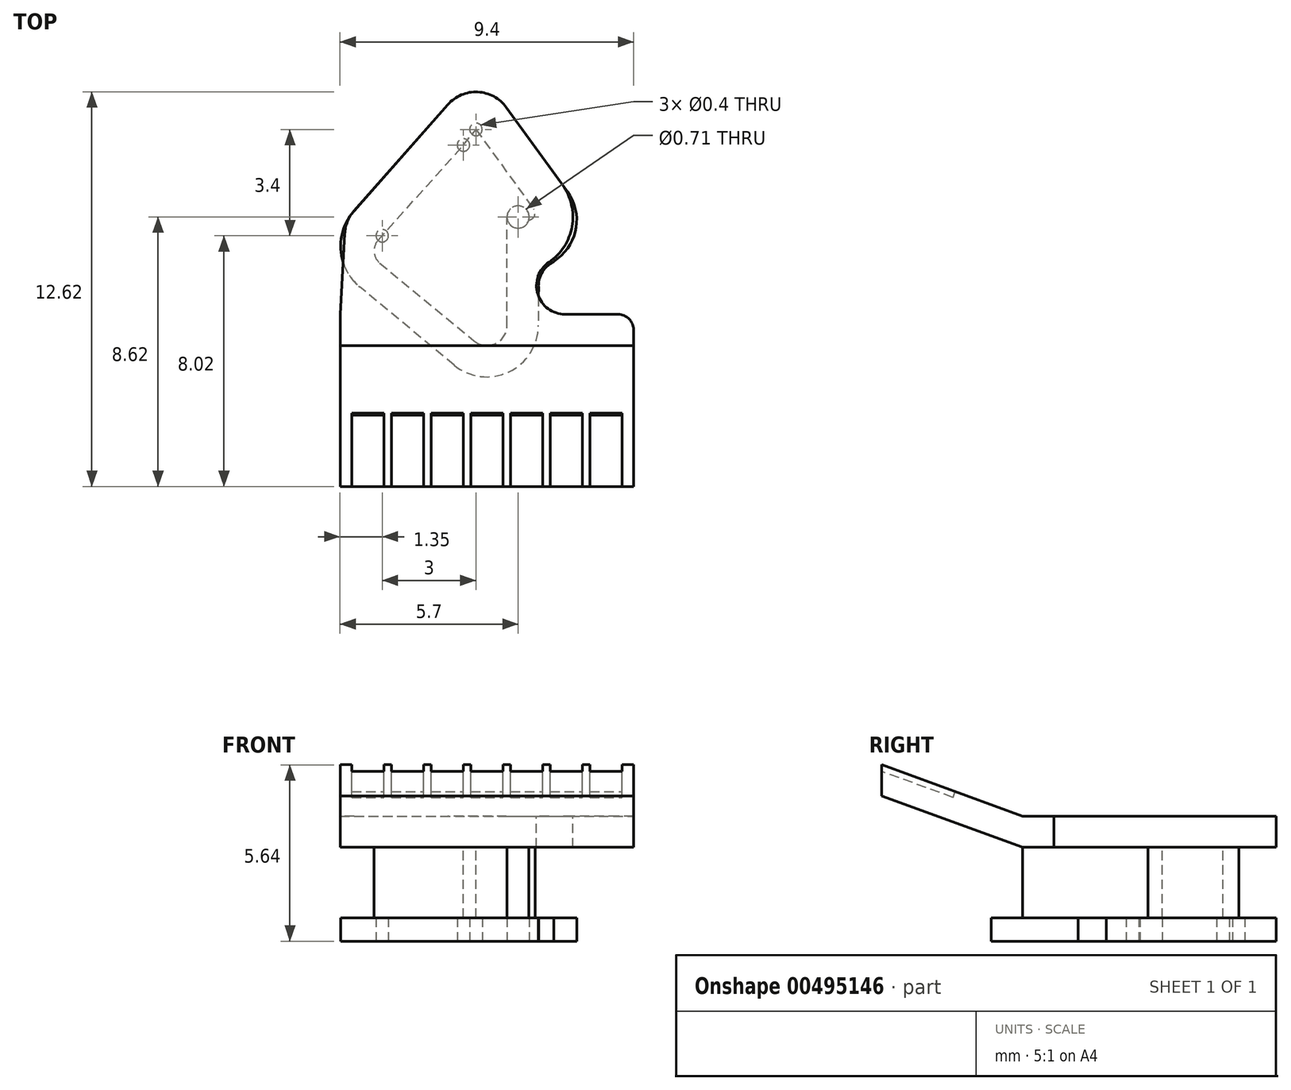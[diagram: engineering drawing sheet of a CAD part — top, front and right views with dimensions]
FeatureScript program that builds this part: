
annotation { "Feature Type Name" : "Feature", "Feature Type Description" : "" }
export const myFeature = defineFeature(function(context is Context, id is Id, definition is map)
    precondition{}
    {
        {
            assignVariable(context, id + "F0", {"name" : "top_height", "anyValue" : 1 * mm});
        }
        {
            assignVariable(context, id + "F1", {"name" : "foot_height", "anyValue" : 0.75 * mm});
        }
        {
            assignVariable(context, id + "F2", {"name" : "total_height", "anyValue" : 4 * mm});
        }
        {
            var Q0;
            Q0=qCreatedBy(makeId("Top.planeOp"),FACE);
            var sketch = newSketch(context, id + "F3", { "sketchPlane" : qUnion([Q0])});
            skCircle(sketch, "E0", {"center": v(-3.35, -1) * mm, "radius": 0.2 * mm});
            skCircle(sketch, "E1", {"center": v(-0.75, 1.9) * mm, "radius": 0.2 * mm});
            skCircle(sketch, "E2", {"center": v(-0.35, 2.4) * mm, "radius": 0.2 * mm});
            skCircle(sketch, "E3", {"center": v(1, -0.4) * mm, "radius": 0.35 * mm});
            skCircle(sketch, "E4", {"center": v(2.5, -2.6) * mm, "radius": 0.85 * mm});
            skSolve(sketch);
        }
        {
            var Q0;
            Q0=qSketchRegion(id+"F3",true);
            extrude(context, id + "F4", {"entities" : qUnion([Q0]), "depth" : getVariable(context, 'total_height')});
        }
        {
            var Q0;
            Q0=makeQuery(id+"F4.opExtrude","CAP_FACE",FACE,{"disambiguationData":[OSD([sQuery(id+"F3.wireOp",EDGE,"E4")])],"isStart":false});
            var sketch = newSketch(context, id + "F5", { "sketchPlane" : qUnion([Q0])});
            skArc(sketch, "E5", {"start": v(2.42, 0.63) * mm, "mid": v(2.72, -0.7) * mm, "end": v(1.99, -1.85) * mm});
            skArc(sketch, "E6", {"start": v(1.99, -1.85) * mm, "mid": v(1.63, -2.87) * mm, "end": v(2.5, -3.51) * mm});
            skArc(sketch, "E7", {"start": v(0.62, 3.1) * mm, "mid": v(-0.3, 3.6) * mm, "end": v(-1.25, 3.2) * mm});
            skArc(sketch, "E8", {"start": v(-4.55, -0.93) * mm, "mid": v(-4.46, -0.54) * mm, "end": v(-4.25, -0.2) * mm});
            skLineSegment(sketch, "E9", {"start": v(-4.25, -0.2) * mm, "end": v(-1.25, 3.2) * mm});
            skLineSegment(sketch, "E10", {"start": v(0.62, 3.1) * mm, "end": v(2.42, 0.63) * mm});
            skLineSegment(sketch, "E11", {"start": v(-4.7, -4.51) * mm, "end": v(4.7, -4.51) * mm});
            skLineSegment(sketch, "E12", {"start": v(-4.7, -4.51) * mm, "end": v(-4.7, -3.51) * mm});
            skLineSegment(sketch, "E13", {"start": v(-4.7, -3.51) * mm, "end": v(-4.55, -0.93) * mm});
            skLineSegment(sketch, "E14", {"start": v(4.7, -4.51) * mm, "end": v(4.7, -4.01) * mm});
            skLineSegment(sketch, "E15", {"start": v(4.2, -3.51) * mm, "end": v(2.5, -3.51) * mm});
            skPoint(sketch, "E16.visualSharp", {"position": v(4.7, -3.51) * mm});
            skArc(sketch, "E16.filletArc", {"start": v(4.7, -4.01) * mm, "mid": v(4.55, -3.66) * mm, "end": v(4.2, -3.51) * mm});
            skLineSegment(sketch, "E17", {"start": v(4.7, -3.51) * mm, "end": v(4.7, -4.51) * mm, "construction": true});
            skSolve(sketch);
        }
        {
            var Q0;
            Q0=qSketchRegion(id+"F5",true);
            extrude(context, id + "F6", {"entities" : qUnion([Q0]), "oppositeDirection" : true, "depth" : getVariable(context, 'top_height')});
        }
        {
            var Q0;
            Q0=makeQuery(id+"F6.opExtrude","CAP_FACE",FACE,{"disambiguationData":[OSD([sQuery(id+"F5.wireOp",EDGE,"E5"),sQuery(id+"F5.wireOp",EDGE,"E6"),sQuery(id+"F5.wireOp",EDGE,"E7"),sQuery(id+"F5.wireOp",EDGE,"E8"),sQuery(id+"F5.wireOp",EDGE,"E9"),sQuery(id+"F5.wireOp",EDGE,"E10"),sQuery(id+"F5.wireOp",EDGE,"E11"),sQuery(id+"F5.wireOp",EDGE,"E12"),sQuery(id+"F5.wireOp",EDGE,"E13"),sQuery(id+"F5.wireOp",EDGE,"E14"),sQuery(id+"F5.wireOp",EDGE,"E15"),sQuery(id+"F5.wireOp",EDGE,"E16.filletArc")])],"isStart":false});
            var sketch = newSketch(context, id + "F7", { "sketchPlane" : qUnion([Q0])});
            skArc(sketch, "E18", {"start": v(-0.41, 4.36) * mm, "mid": v(0.27, 4.45) * mm, "end": v(0.64, 3.87) * mm});
            skLineSegment(sketch, "E19", {"start": v(0.64, 3.87) * mm, "end": v(0.64, 0.4) * mm});
            skArc(sketch, "E20", {"start": v(0.64, 0.4) * mm, "mid": v(1.05, 0.05) * mm, "end": v(1.34, 0.5) * mm});
            skLineSegment(sketch, "E21", {"start": v(-3.48, 1.15) * mm, "end": v(-0.75, -1.9) * mm});
            skPoint(sketch, "E22", {"position": v(-3.35, 1) * mm});
            skPoint(sketch, "E23", {"position": v(-0.75, -1.9) * mm});
            skPoint(sketch, "E24", {"position": v(-0.35, -2.4) * mm});
            skLineSegment(sketch, "E25", {"start": v(-0.75, -1.9) * mm, "end": v(-0.35, -2.4) * mm});
            skArc(sketch, "E26", {"start": v(-3.48, 1.15) * mm, "mid": v(-3.6, 1.52) * mm, "end": v(-3.43, 1.87) * mm});
            skLineSegment(sketch, "E27", {"start": v(-3.43, 1.87) * mm, "end": v(-0.41, 4.36) * mm});
            skLineSegment(sketch, "E28", {"start": v(-0.35, -2.4) * mm, "end": v(1.5, 0.15) * mm});
            skArc(sketch, "E29", {"start": v(1.5, 0.15) * mm, "mid": v(1.52, 0.37) * mm, "end": v(1.34, 0.5) * mm});
            skSolve(sketch);
        }
        {
            var Q0;
            Q0=qSketchRegion(id+"F7",true);
            extrude(context, id + "F8", {"entities" : qUnion([Q0]), "depth" : getVariable(context, 'total_height') - getVariable(context, 'top_height') - getVariable(context, 'foot_height')});
        }
        {
            var Q0;
            Q0=makeQuery(id+"F8.opExtrude","CAP_FACE",FACE,{"disambiguationData":[OSD([sQuery(id+"F7.wireOp",EDGE,"E18"),sQuery(id+"F7.wireOp",EDGE,"E19"),sQuery(id+"F7.wireOp",EDGE,"E20"),sQuery(id+"F7.wireOp",EDGE,"E21"),sQuery(id+"F7.wireOp",EDGE,"E25"),sQuery(id+"F7.wireOp",EDGE,"E26"),sQuery(id+"F7.wireOp",EDGE,"E27"),sQuery(id+"F7.wireOp",EDGE,"N2l6SWo4-kHqm-KqNM-dVRS-lvh92gExjqxJ"),sQuery(id+"F7.wireOp",EDGE,"E28"),sQuery(id+"F7.wireOp",EDGE,"JDNASti5-YGJY-wVQ3-qJS6-gXQv6eLAw1aX")])],"isStart":false});
            var sketch = newSketch(context, id + "F9", { "sketchPlane" : qUnion([Q0])});
            skLineSegment(sketch, "E30", {"start": v(-4.26, 0.21) * mm, "end": v(-1.25, -3.2) * mm});
            skLineSegment(sketch, "E31", {"start": v(0.62, -3.1) * mm, "end": v(2.58, -0.4) * mm});
            skLineSegment(sketch, "E32", {"start": v(1.65, 2.96) * mm, "end": v(1.65, 3.87) * mm});
            skLineSegment(sketch, "E33", {"start": v(-1.05, 5.14) * mm, "end": v(-4.07, 2.64) * mm});
            skArc(sketch, "E34.filletArc", {"start": v(-4.07, 2.64) * mm, "mid": v(-4.68, 1.47) * mm, "end": v(-4.26, 0.21) * mm});
            skPoint(sketch, "E35.visualSharp", {"position": v(1.65, 7.36) * mm});
            skArc(sketch, "E35.filletArc", {"start": v(1.65, 3.87) * mm, "mid": v(0.7, 5.36) * mm, "end": v(-1.05, 5.14) * mm});
            skArc(sketch, "E36.filletArc", {"start": v(2.58, -0.4) * mm, "mid": v(2.86, 0.73) * mm, "end": v(2.26, 1.73) * mm});
            skArc(sketch, "E37.filletArc", {"start": v(1.65, 2.96) * mm, "mid": v(1.8, 2.27) * mm, "end": v(2.26, 1.73) * mm});
            skPoint(sketch, "E38.visualSharp", {"position": v(-0.26, -4.32) * mm});
            skArc(sketch, "E38.filletArc", {"start": v(-1.25, -3.2) * mm, "mid": v(-0.3, -3.6) * mm, "end": v(0.62, -3.1) * mm});
            skSolve(sketch);
        }
        {
            var Q0;
            Q0=qSketchRegion(id+"F9",true);
            extrude(context, id + "F10", {"entities" : qUnion([Q0]), "depth" : getVariable(context, 'foot_height')});
        }
        {
            var Q0;
            Q0=makeQuery(id+"F4.opExtrude","SWEPT_BODY",BODY,{"disambiguationData":[OSD([sQuery(id+"F3.wireOp",EDGE,"E0")])]});
            var Q1;
            Q1=makeQuery(id+"F4.opExtrude","SWEPT_BODY",BODY,{"disambiguationData":[OSD([sQuery(id+"F3.wireOp",EDGE,"E1")])]});
            var Q2;
            Q2=makeQuery(id+"F4.opExtrude","SWEPT_BODY",BODY,{"disambiguationData":[OSD([sQuery(id+"F3.wireOp",EDGE,"E2")])]});
            var Q3;
            Q3=makeQuery(id+"F4.opExtrude","SWEPT_BODY",BODY,{"disambiguationData":[OSD([sQuery(id+"F3.wireOp",EDGE,"E3")])]});
            var Q4;
            Q4=makeQuery(id+"F4.opExtrude","SWEPT_BODY",BODY,{"disambiguationData":[OSD([sQuery(id+"F3.wireOp",EDGE,"E4")])]});
            var Q5;
            Q5=makeQuery(id+"F10.opExtrude","SWEPT_BODY",BODY,{"disambiguationData":[OSD([sQuery(id+"F9.wireOp",EDGE,"E30"),sQuery(id+"F9.wireOp",EDGE,"E31"),sQuery(id+"F9.wireOp",EDGE,"E32"),sQuery(id+"F9.wireOp",EDGE,"E33"),sQuery(id+"F9.wireOp",EDGE,"E34.filletArc"),sQuery(id+"F9.wireOp",EDGE,"E35.filletArc"),sQuery(id+"F9.wireOp",EDGE,"E36.filletArc"),sQuery(id+"F9.wireOp",EDGE,"E37.filletArc"),sQuery(id+"F9.wireOp",EDGE,"E38.filletArc")])]});
            booleanBodies(context, id + "F11", {"operationType" : BooleanOperationType.SUBTRACTION, "tools" : qUnion([Q0, Q1, Q2, Q3, Q4]), "targets" : qUnion([Q5])});
        }
        {
            var Q0;
            Q0=qCreatedBy(makeId("Right.planeOp"),FACE);
            var sketch = newSketch(context, id + "F12", { "sketchPlane" : qUnion([Q0])});
            skLineSegment(sketch, "E39", {"start": v(-9.02, 5.64) * mm, "end": v(-4.51, 4) * mm});
            skSolve(sketch);
        }
        {
            var Q0;
            Q0=makeQuery(id+"F6.opExtrude","SWEPT_FACE",FACE,{"disambiguationData":[OSD([sQuery(id+"F5.wireOp",EDGE,"E11")])]});
            var Q1;
            Q1=sQuery(id+"F12.wireOp",EDGE,"E39");
            sweep(context, id + "F13", {"operationType" : NewBodyOperationType.ADD, "profiles" : qUnion([Q0]), "path" : qUnion([Q1]), "keepProfileOrientation" : true});
        }
        {
            var Q0;
            {var subQ0=sQuery(id+"F12.wireOp",EDGE,"E39");var subQ1=sQuery(id+"F5.wireOp",EDGE,"E11");Q0=makeQuery(id+"F13.opSweep","SWEPT_FACE",FACE,{"disambiguationData":[OSD([subQ1,subQ0]),TDD([makeQuery(id+"F6.opExtrude","CAP_EDGE",EDGE,{"disambiguationData":[OSD([subQ1])],"isStart":true}),subQ0])]});}
            var sketch = newSketch(context, id + "F14", { "sketchPlane" : qUnion([Q0])});
            skLineSegment(sketch, "E40.bottom", {"start": v(-4.32, -7.9) * mm, "end": v(-3.3, -7.9) * mm});
            skLineSegment(sketch, "E40.top", {"start": v(-4.32, -10.4) * mm, "end": v(-3.3, -10.4) * mm});
            skLineSegment(sketch, "E40.left", {"start": v(-4.32, -7.9) * mm, "end": v(-4.32, -10.4) * mm});
            skLineSegment(sketch, "E40.right", {"start": v(-3.3, -7.9) * mm, "end": v(-3.3, -10.4) * mm});
            skLineSegment(sketch, "E41.1.0.0", {"start": v(-3.05, -7.9) * mm, "end": v(-3.05, -10.4) * mm});
            skLineSegment(sketch, "E41.1.0.1", {"start": v(-3.05, -7.9) * mm, "end": v(-2.03, -7.9) * mm});
            skLineSegment(sketch, "E41.1.0.2", {"start": v(-2.03, -7.9) * mm, "end": v(-2.03, -10.4) * mm});
            skLineSegment(sketch, "E41.1.0.3", {"start": v(-3.05, -10.4) * mm, "end": v(-2.03, -10.4) * mm});
            skLineSegment(sketch, "E41.2.0.0", {"start": v(-1.78, -7.9) * mm, "end": v(-1.78, -10.4) * mm});
            skLineSegment(sketch, "E41.2.0.1", {"start": v(-1.78, -7.9) * mm, "end": v(-0.76, -7.9) * mm});
            skLineSegment(sketch, "E41.2.0.2", {"start": v(-0.76, -7.9) * mm, "end": v(-0.76, -10.4) * mm});
            skLineSegment(sketch, "E41.2.0.3", {"start": v(-1.78, -10.4) * mm, "end": v(-0.76, -10.4) * mm});
            skLineSegment(sketch, "E41.3.0.0", {"start": v(-0.51, -7.9) * mm, "end": v(-0.51, -10.4) * mm});
            skLineSegment(sketch, "E41.3.0.1", {"start": v(-0.5, -7.9) * mm, "end": v(0.51, -7.9) * mm});
            skLineSegment(sketch, "E41.3.0.2", {"start": v(0.51, -7.9) * mm, "end": v(0.51, -10.4) * mm});
            skLineSegment(sketch, "E41.3.0.3", {"start": v(-0.5, -10.4) * mm, "end": v(0.51, -10.4) * mm});
            skLineSegment(sketch, "E41.4.0.0", {"start": v(0.76, -7.9) * mm, "end": v(0.76, -10.4) * mm});
            skLineSegment(sketch, "E41.4.0.1", {"start": v(0.76, -7.9) * mm, "end": v(1.78, -7.9) * mm});
            skLineSegment(sketch, "E41.4.0.2", {"start": v(1.78, -7.9) * mm, "end": v(1.78, -10.4) * mm});
            skLineSegment(sketch, "E41.4.0.3", {"start": v(0.76, -10.4) * mm, "end": v(1.78, -10.4) * mm});
            skLineSegment(sketch, "E41.5.0.0", {"start": v(2.03, -7.9) * mm, "end": v(2.03, -10.4) * mm});
            skLineSegment(sketch, "E41.5.0.1", {"start": v(2.03, -7.9) * mm, "end": v(3.05, -7.9) * mm});
            skLineSegment(sketch, "E41.5.0.2", {"start": v(3.05, -7.9) * mm, "end": v(3.05, -10.4) * mm});
            skLineSegment(sketch, "E41.5.0.3", {"start": v(2.03, -10.4) * mm, "end": v(3.05, -10.4) * mm});
            skLineSegment(sketch, "E41.6.0.0", {"start": v(3.3, -7.9) * mm, "end": v(3.3, -10.4) * mm});
            skLineSegment(sketch, "E41.6.0.1", {"start": v(3.3, -7.9) * mm, "end": v(4.32, -7.9) * mm});
            skLineSegment(sketch, "E41.6.0.2", {"start": v(4.32, -7.9) * mm, "end": v(4.32, -10.4) * mm});
            skLineSegment(sketch, "E41.6.0.3", {"start": v(3.3, -10.4) * mm, "end": v(4.32, -10.4) * mm});
            skLineSegment(sketch, "E41.direction1", {"start": v(-4.32, -10.4) * mm, "end": v(-3.05, -10.4) * mm, "construction": true});
            skSolve(sketch);
        }
        {
            var Q0;
            Q0=qSketchRegion(id+"F14",true);
            extrude(context, id + "F15", {"entities" : qUnion([Q0]), "operationType" : NewBodyOperationType.REMOVE, "oppositeDirection" : true, "depth" : 0.2 * mm});
        }
    });
